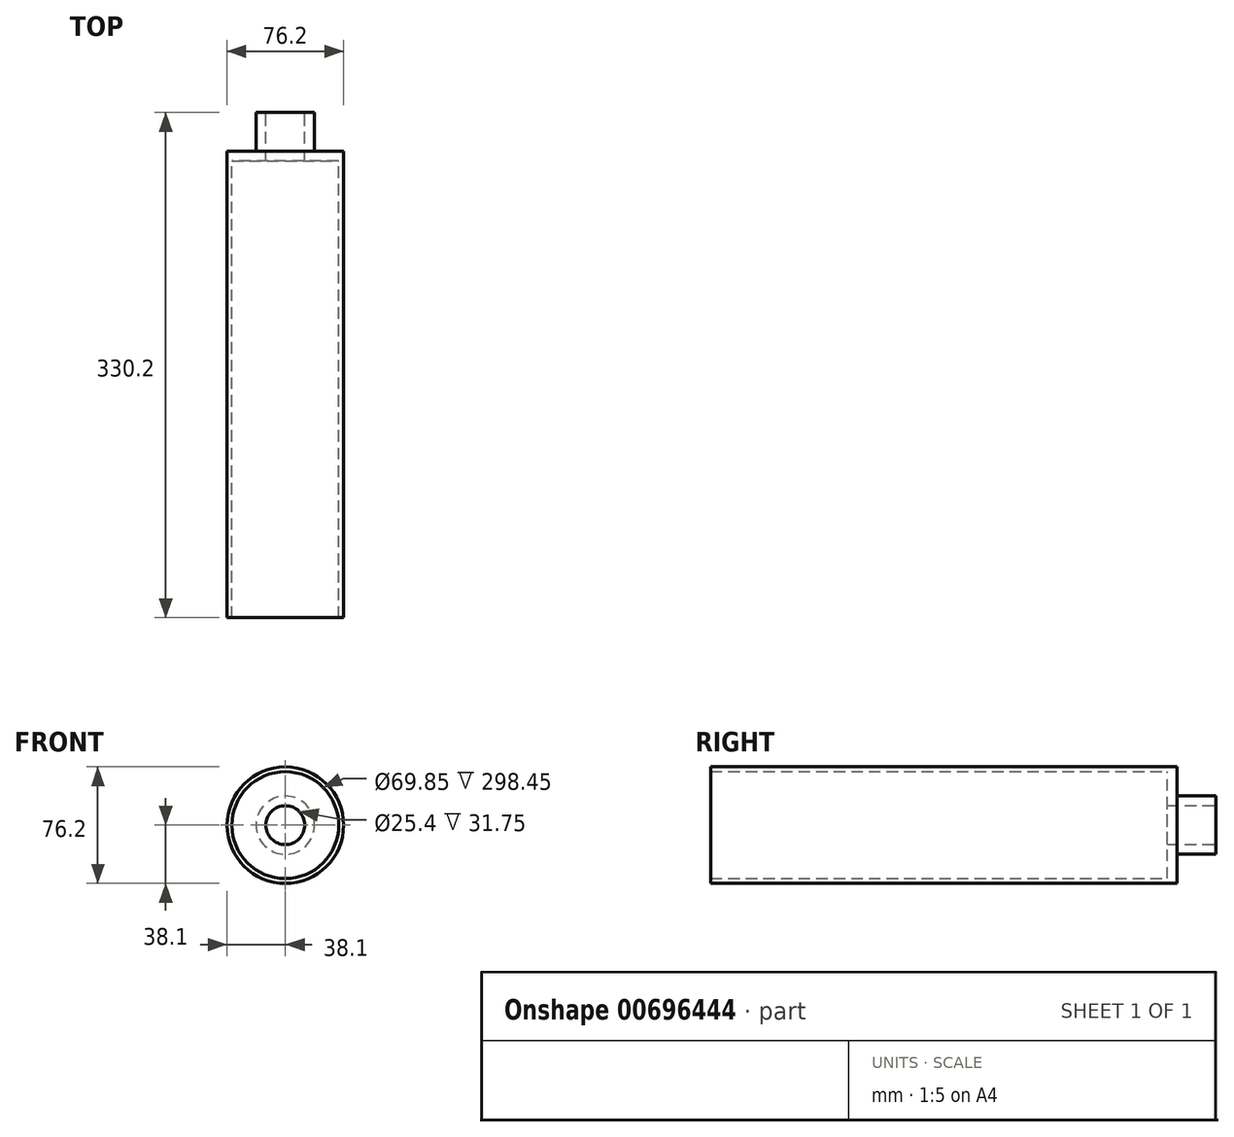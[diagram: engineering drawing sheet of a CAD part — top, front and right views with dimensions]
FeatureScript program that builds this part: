
annotation { "Feature Type Name" : "Feature", "Feature Type Description" : "" }
export const myFeature = defineFeature(function(context is Context, id is Id, definition is map)
    precondition{}
    {
        {
            var Q0;
            Q0=qCreatedBy(makeId("Front.planeOp"),FACE);
            var sketch = newSketch(context, id + "F0", { "sketchPlane" : qUnion([Q0])});
            skCircle(sketch, "E0", {"center": v(0, 0) * mm, "radius": 38.1 * mm});
            skCircle(sketch, "E1", {"center": v(0, 0) * mm, "radius": 34.93 * mm});
            skSolve(sketch);
        }
        {
            var Q0;
            Q0=makeQuery(id+"F0.imprint","IMPRINT",FACE,{"disambiguationData":[TD([[makeQuery(id+"F0.imprint","IMPRINT",EDGE,{"derivedFrom":sQuery(id+"F0.wireOp",EDGE,"E0")}),1.0]])]});
            extrude(context, id + "F1", {"entities" : qUnion([Q0]), "depth" : 304.8 * mm, "offsetDistance" : 25.4 * mm});
        }
        {
            var Q0;
            Q0=makeQuery(id+"F0.imprint","IMPRINT",FACE,{"disambiguationData":[TD([[makeQuery(id+"F0.imprint","IMPRINT",EDGE,{"derivedFrom":sQuery(id+"F0.wireOp",EDGE,"E1")}),1.0]])]});
            extrude(context, id + "F2", {"entities" : qUnion([Q0]), "operationType" : NewBodyOperationType.ADD, "depth" : 6.35 * mm, "offsetDistance" : 25.4 * mm});
        }
        {
            var Q0;
            Q0=makeQuery(id+"F0.imprint","IMPRINT",FACE,{"disambiguationData":[TD([[makeQuery(id+"F0.imprint","IMPRINT",EDGE,{"derivedFrom":sQuery(id+"F0.wireOp",EDGE,"E1")}),1.0]])]});
            var sketch = newSketch(context, id + "F3", { "sketchPlane" : qUnion([Q0])});
            skCircle(sketch, "E2", {"center": v(0, 0) * mm, "radius": 19.05 * mm});
            skSolve(sketch);
        }
        {
            var Q0;
            Q0=makeQuery(id+"F3.imprint","IMPRINT",FACE,{"disambiguationData":[TD([[makeQuery(id+"F3.imprint","IMPRINT",EDGE,{"derivedFrom":sQuery(id+"F3.wireOp",EDGE,"E2")}),1.0]])]});
            extrude(context, id + "F4", {"entities" : qUnion([Q0]), "operationType" : NewBodyOperationType.ADD, "oppositeDirection" : true, "depth" : 25.4 * mm, "offsetDistance" : 25.4 * mm});
        }
        {
            var Q0;
            Q0=makeQuery(id+"F4.opExtrude","CAP_FACE",FACE,{"disambiguationData":[OSD([sQuery(id+"F3.wireOp",EDGE,"E2")])],"isStart":false});
            var sketch = newSketch(context, id + "F5", { "sketchPlane" : qUnion([Q0])});
            skPoint(sketch, "E3", {"position": v(0, 0) * mm});
            skSolve(sketch);
        }
        {
            var Q0;
            Q0=sQuery(id+"F5.wireOp",VERTEX,"E3");
            var Q1;
            Q1=makeQuery(id+"F1.opExtrude","SWEPT_BODY",BODY,{"disambiguationData":[OSD([sQuery(id+"F0.wireOp",EDGE,"E0"),sQuery(id+"F0.wireOp",EDGE,"E1")])]});
            hole(context, id + "F6", {"style" : HoleStyle.SIMPLE, "endStyle" : HoleEndStyle.BLIND, "holeDiameter" : 25.4 * mm, "majorDiameter" : 6.35 * mm, "holeDepth" : 38.1 * mm, "isTappedThrough" : true, "tappedDepth" : 12.7 * mm, "tapClearance" : 3, "startFromSketch" : true, "locations" : qUnion([Q0]), "scope" : qUnion([Q1])});
        }
    });
